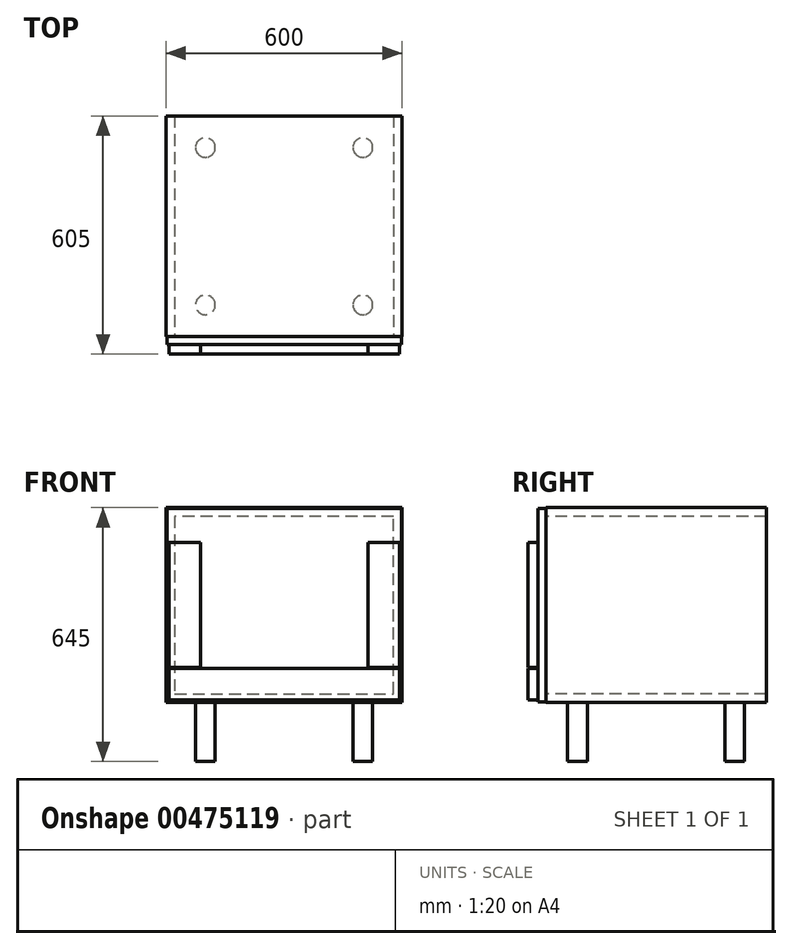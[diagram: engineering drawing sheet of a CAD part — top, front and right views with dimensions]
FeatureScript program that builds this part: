
annotation { "Feature Type Name" : "Feature", "Feature Type Description" : "" }
export const myFeature = defineFeature(function(context is Context, id is Id, definition is map)
    precondition{}
    {
        {
            var Q0;
            Q0=qCreatedBy(makeId("Top.planeOp"),FACE);
            var sketch = newSketch(context, id + "F0", { "sketchPlane" : qUnion([Q0])});
            skLineSegment(sketch, "E0.bottom", {"start": v(-300, 280) * mm, "end": v(300, 280) * mm});
            skLineSegment(sketch, "E0.top", {"start": v(-300, -280) * mm, "end": v(300, -280) * mm});
            skLineSegment(sketch, "E0.left", {"start": v(-300, 280) * mm, "end": v(-300, -280) * mm});
            skLineSegment(sketch, "E0.right", {"start": v(300, 280) * mm, "end": v(300, -280) * mm});
            skPoint(sketch, "E0.middle", {"position": v(0, 0) * mm});
            skSolve(sketch);
        }
        {
            var Q0;
            Q0=qSketchRegion(id+"F0",true);
            extrude(context, id + "F1", {"entities" : qUnion([Q0]), "depth" : 495 * mm, "offsetDistance" : 25 * mm});
        }
        {
            var Q0;
            Q0=makeQuery(id+"F1.opExtrude","SWEPT_FACE",FACE,{"disambiguationData":[OSD([sQuery(id+"F0.wireOp",EDGE,"E0.top")])]});
            var sketch = newSketch(context, id + "F2", { "sketchPlane" : qUnion([Q0])});
            skLineSegment(sketch, "E1.0", {"start": v(-278, 22) * mm, "end": v(278, 22) * mm});
            skLineSegment(sketch, "E1.1", {"start": v(-278, 473) * mm, "end": v(-278, 22) * mm});
            skLineSegment(sketch, "E1.2", {"start": v(278, 473) * mm, "end": v(-278, 473) * mm});
            skLineSegment(sketch, "E1.3", {"start": v(278, 22) * mm, "end": v(278, 473) * mm});
            skSolve(sketch);
        }
        {
            var Q0;
            Q0=makeQuery(id+"F2.imprint","IMPRINT",FACE,{"disambiguationData":[TD([[makeQuery(id+"F2.imprint","IMPRINT",EDGE,{"derivedFrom":sQuery(id+"F2.wireOp",EDGE,"E1.0")}),1.0]])]});
            extrude(context, id + "F3", {"entities" : qUnion([Q0]), "operationType" : NewBodyOperationType.REMOVE, "endBound" : BoundingType.UP_TO_NEXT, "oppositeDirection" : true, "depth" : 25 * mm, "offsetDistance" : 25 * mm});
        }
        {
            var Q0;
            Q0=makeQuery(id+"F1.opExtrude","CAP_FACE",FACE,{"disambiguationData":[OSD([sQuery(id+"F0.wireOp",EDGE,"E0.bottom"),sQuery(id+"F0.wireOp",EDGE,"E0.top"),sQuery(id+"F0.wireOp",EDGE,"E0.left"),sQuery(id+"F0.wireOp",EDGE,"E0.right")])],"isStart":true});
            var sketch = newSketch(context, id + "F4", { "sketchPlane" : qUnion([Q0])});
            skLineSegment(sketch, "E2.bottom", {"start": v(200, 200) * mm, "end": v(-200, 200) * mm});
            skLineSegment(sketch, "E2.top", {"start": v(200, -200) * mm, "end": v(-200, -200) * mm});
            skLineSegment(sketch, "E2.left", {"start": v(200, 200) * mm, "end": v(200, -200) * mm});
            skLineSegment(sketch, "E2.right", {"start": v(-200, 200) * mm, "end": v(-200, -200) * mm});
            skPoint(sketch, "E2.middle", {"position": v(0, 0) * mm});
            skCircle(sketch, "E3", {"center": v(-200, 200) * mm, "radius": 25 * mm});
            skCircle(sketch, "E4", {"center": v(200, 200) * mm, "radius": 25 * mm});
            skCircle(sketch, "E5", {"center": v(200, -200) * mm, "radius": 25 * mm});
            skCircle(sketch, "E6", {"center": v(-200, -200) * mm, "radius": 25 * mm});
            skSolve(sketch);
        }
        {
            var Q0;
            {var subQ0=sQuery(id+"F4.wireOp",EDGE,"E2.right");var subQ1=sQuery(id+"F4.wireOp",EDGE,"E2.bottom");var subQ2=makeQuery(id+"F4.imprint","INTERSECT",VERTEX,{"derivedFrom":[subQ1,subQ0]});Q0=makeQuery(id+"F4.imprint","IMPRINT",FACE,{"disambiguationData":[TD([[makeQuery(id+"F4.imprint","IMPRINT",EDGE,{"disambiguationData":[TD([[subQ2,1.0]])],"derivedFrom":subQ1}),1.0]])]});}
            var Q1;
            {var subQ0=sQuery(id+"F4.wireOp",EDGE,"E2.right");var subQ1=sQuery(id+"F4.wireOp",EDGE,"E2.bottom");var subQ2=makeQuery(id+"F4.imprint","INTERSECT",VERTEX,{"derivedFrom":[subQ1,subQ0]});Q1=makeQuery(id+"F4.imprint","IMPRINT",FACE,{"disambiguationData":[TD([[makeQuery(id+"F4.imprint","IMPRINT",EDGE,{"disambiguationData":[TD([[subQ2,1.0]])],"derivedFrom":subQ1}),-1.0]])]});}
            var Q2;
            {var subQ0=sQuery(id+"F4.wireOp",EDGE,"E2.left");var subQ1=sQuery(id+"F4.wireOp",EDGE,"E2.bottom");var subQ2=makeQuery(id+"F4.imprint","INTERSECT",VERTEX,{"derivedFrom":[subQ1,subQ0]});Q2=makeQuery(id+"F4.imprint","IMPRINT",FACE,{"disambiguationData":[TD([[makeQuery(id+"F4.imprint","IMPRINT",EDGE,{"disambiguationData":[TD([[subQ2,-1.0]])],"derivedFrom":subQ1}),-1.0]])]});}
            var Q3;
            {var subQ0=sQuery(id+"F4.wireOp",EDGE,"E2.left");var subQ1=sQuery(id+"F4.wireOp",EDGE,"E2.bottom");var subQ2=makeQuery(id+"F4.imprint","INTERSECT",VERTEX,{"derivedFrom":[subQ1,subQ0]});Q3=makeQuery(id+"F4.imprint","IMPRINT",FACE,{"disambiguationData":[TD([[makeQuery(id+"F4.imprint","IMPRINT",EDGE,{"disambiguationData":[TD([[subQ2,-1.0]])],"derivedFrom":subQ1}),1.0]])]});}
            var Q4;
            {var subQ0=sQuery(id+"F4.wireOp",EDGE,"E2.left");var subQ1=sQuery(id+"F4.wireOp",EDGE,"E2.top");var subQ2=makeQuery(id+"F4.imprint","INTERSECT",VERTEX,{"derivedFrom":[subQ1,subQ0]});Q4=makeQuery(id+"F4.imprint","IMPRINT",FACE,{"disambiguationData":[TD([[makeQuery(id+"F4.imprint","IMPRINT",EDGE,{"disambiguationData":[TD([[subQ2,-1.0]])],"derivedFrom":subQ1}),1.0]])]});}
            var Q5;
            {var subQ0=sQuery(id+"F4.wireOp",EDGE,"E2.left");var subQ1=sQuery(id+"F4.wireOp",EDGE,"E2.top");var subQ2=makeQuery(id+"F4.imprint","INTERSECT",VERTEX,{"derivedFrom":[subQ1,subQ0]});Q5=makeQuery(id+"F4.imprint","IMPRINT",FACE,{"disambiguationData":[TD([[makeQuery(id+"F4.imprint","IMPRINT",EDGE,{"disambiguationData":[TD([[subQ2,-1.0]])],"derivedFrom":subQ1}),-1.0]])]});}
            var Q6;
            {var subQ0=sQuery(id+"F4.wireOp",EDGE,"E2.right");var subQ1=sQuery(id+"F4.wireOp",EDGE,"E2.top");var subQ2=makeQuery(id+"F4.imprint","INTERSECT",VERTEX,{"derivedFrom":[subQ1,subQ0]});Q6=makeQuery(id+"F4.imprint","IMPRINT",FACE,{"disambiguationData":[TD([[makeQuery(id+"F4.imprint","IMPRINT",EDGE,{"disambiguationData":[TD([[subQ2,1.0]])],"derivedFrom":subQ1}),1.0]])]});}
            var Q7;
            {var subQ0=sQuery(id+"F4.wireOp",EDGE,"E2.right");var subQ1=sQuery(id+"F4.wireOp",EDGE,"E2.top");var subQ2=makeQuery(id+"F4.imprint","INTERSECT",VERTEX,{"derivedFrom":[subQ1,subQ0]});Q7=makeQuery(id+"F4.imprint","IMPRINT",FACE,{"disambiguationData":[TD([[makeQuery(id+"F4.imprint","IMPRINT",EDGE,{"disambiguationData":[TD([[subQ2,1.0]])],"derivedFrom":subQ1}),-1.0]])]});}
            extrude(context, id + "F5", {"entities" : qUnion([Q0, Q1, Q2, Q3, Q4, Q5, Q6, Q7]), "operationType" : NewBodyOperationType.ADD, "depth" : 150 * mm, "offsetDistance" : 25 * mm});
        }
        {
            var Q0;
            Q0=makeQuery(id+"F1.opExtrude","SWEPT_FACE",FACE,{"disambiguationData":[OSD([sQuery(id+"F0.wireOp",EDGE,"E0.top")])]});
            var sketch = newSketch(context, id + "F6", { "sketchPlane" : qUnion([Q0])});
            skLineSegment(sketch, "E7.0", {"start": v(-298, 493) * mm, "end": v(298, 493) * mm});
            skLineSegment(sketch, "E7.1", {"start": v(-298, 493) * mm, "end": v(-298, 2) * mm});
            skLineSegment(sketch, "E7.2", {"start": v(-298, 2) * mm, "end": v(298, 2) * mm});
            skLineSegment(sketch, "E7.3", {"start": v(298, 493) * mm, "end": v(298, 2) * mm});
            skSolve(sketch);
        }
        {
            var Q0;
            Q0=qSketchRegion(id+"F6",true);
            extrude(context, id + "F7", {"entities" : qUnion([Q0]), "operationType" : NewBodyOperationType.ADD, "depth" : 20 * mm, "offsetDistance" : 25 * mm});
        }
        {
            var Q0;
            Q0=makeQuery(id+"F7.opExtrude","CAP_FACE",FACE,{"disambiguationData":[OSD([sQuery(id+"F6.wireOp",EDGE,"E7.0"),sQuery(id+"F6.wireOp",EDGE,"E7.1"),sQuery(id+"F6.wireOp",EDGE,"E7.2"),sQuery(id+"F6.wireOp",EDGE,"E7.3")])],"isStart":false});
            var sketch = newSketch(context, id + "F8", { "sketchPlane" : qUnion([Q0])});
            skLineSegment(sketch, "E8.0", {"start": v(293, 7) * mm, "end": v(293, 488) * mm});
            skLineSegment(sketch, "E8.1", {"start": v(-293, 7) * mm, "end": v(293, 7) * mm});
            skLineSegment(sketch, "E8.2", {"start": v(-293, 488) * mm, "end": v(-293, 7) * mm});
            skLineSegment(sketch, "E8.3", {"start": v(293, 488) * mm, "end": v(-293, 488) * mm});
            skLineSegment(sketch, "E9.bottom", {"start": v(-293, 488) * mm, "end": v(293, 488) * mm});
            skLineSegment(sketch, "E9.top", {"start": v(-293, 408) * mm, "end": v(293, 408) * mm});
            skLineSegment(sketch, "E9.left", {"start": v(-293, 488) * mm, "end": v(-293, 408) * mm});
            skLineSegment(sketch, "E9.right", {"start": v(293, 488) * mm, "end": v(293, 408) * mm});
            skLineSegment(sketch, "E10.top", {"start": v(-293, 87) * mm, "end": v(293, 87) * mm});
            skLineSegment(sketch, "E10.left", {"start": v(-293, 7) * mm, "end": v(-293, 87) * mm});
            skLineSegment(sketch, "E10.right", {"start": v(293, 7) * mm, "end": v(293, 87) * mm});
            skLineSegment(sketch, "E11.bottom", {"start": v(213, 406.5) * mm, "end": v(293, 406.5) * mm});
            skLineSegment(sketch, "E11.top", {"start": v(213, 88.5) * mm, "end": v(293, 88.5) * mm});
            skLineSegment(sketch, "E11.left", {"start": v(213, 406.5) * mm, "end": v(213, 88.5) * mm});
            skLineSegment(sketch, "E11.right", {"start": v(293, 406.5) * mm, "end": v(293, 88.5) * mm});
            skLineSegment(sketch, "E12.bottom", {"start": v(-293, 88.5) * mm, "end": v(-213, 88.5) * mm});
            skLineSegment(sketch, "E12.top", {"start": v(-293, 406.5) * mm, "end": v(-213, 406.5) * mm});
            skLineSegment(sketch, "E12.left", {"start": v(-293, 88.5) * mm, "end": v(-293, 406.5) * mm});
            skLineSegment(sketch, "E12.right", {"start": v(-213, 88.5) * mm, "end": v(-213, 406.5) * mm});
            skSolve(sketch);
        }
        {
            var Q0;
            Q0=makeQuery(id+"F8.imprint","IMPRINT",FACE,{"disambiguationData":[TD([[makeQuery(id+"F8.imprint","IMPRINT",EDGE,{"derivedFrom":sQuery(id+"F8.wireOp",EDGE,"E9.bottom")}),-1.0]])]});
            var Q1;
            Q1=makeQuery(id+"F8.imprint","IMPRINT",FACE,{"disambiguationData":[TD([[makeQuery(id+"F8.imprint","IMPRINT",EDGE,{"derivedFrom":sQuery(id+"F8.wireOp",EDGE,"E12.bottom")}),1.0]])]});
            var Q2;
            Q2=makeQuery(id+"F8.imprint","IMPRINT",FACE,{"disambiguationData":[TD([[makeQuery(id+"F8.imprint","IMPRINT",EDGE,{"derivedFrom":sQuery(id+"F8.wireOp",EDGE,"E11.bottom")}),-1.0]])]});
            var Q3;
            Q3=makeQuery(id+"F8.imprint","IMPRINT",FACE,{"disambiguationData":[TD([[makeQuery(id+"F8.imprint","IMPRINT",EDGE,{"derivedFrom":sQuery(id+"F8.wireOp",EDGE,"E8.1")}),1.0]])]});
            extrude(context, id + "F9", {"entities" : qUnion([Q0, Q1, Q2, Q3]), "operationType" : NewBodyOperationType.ADD, "depth" : 25 * mm, "offsetDistance" : 25 * mm});
        }
    });
